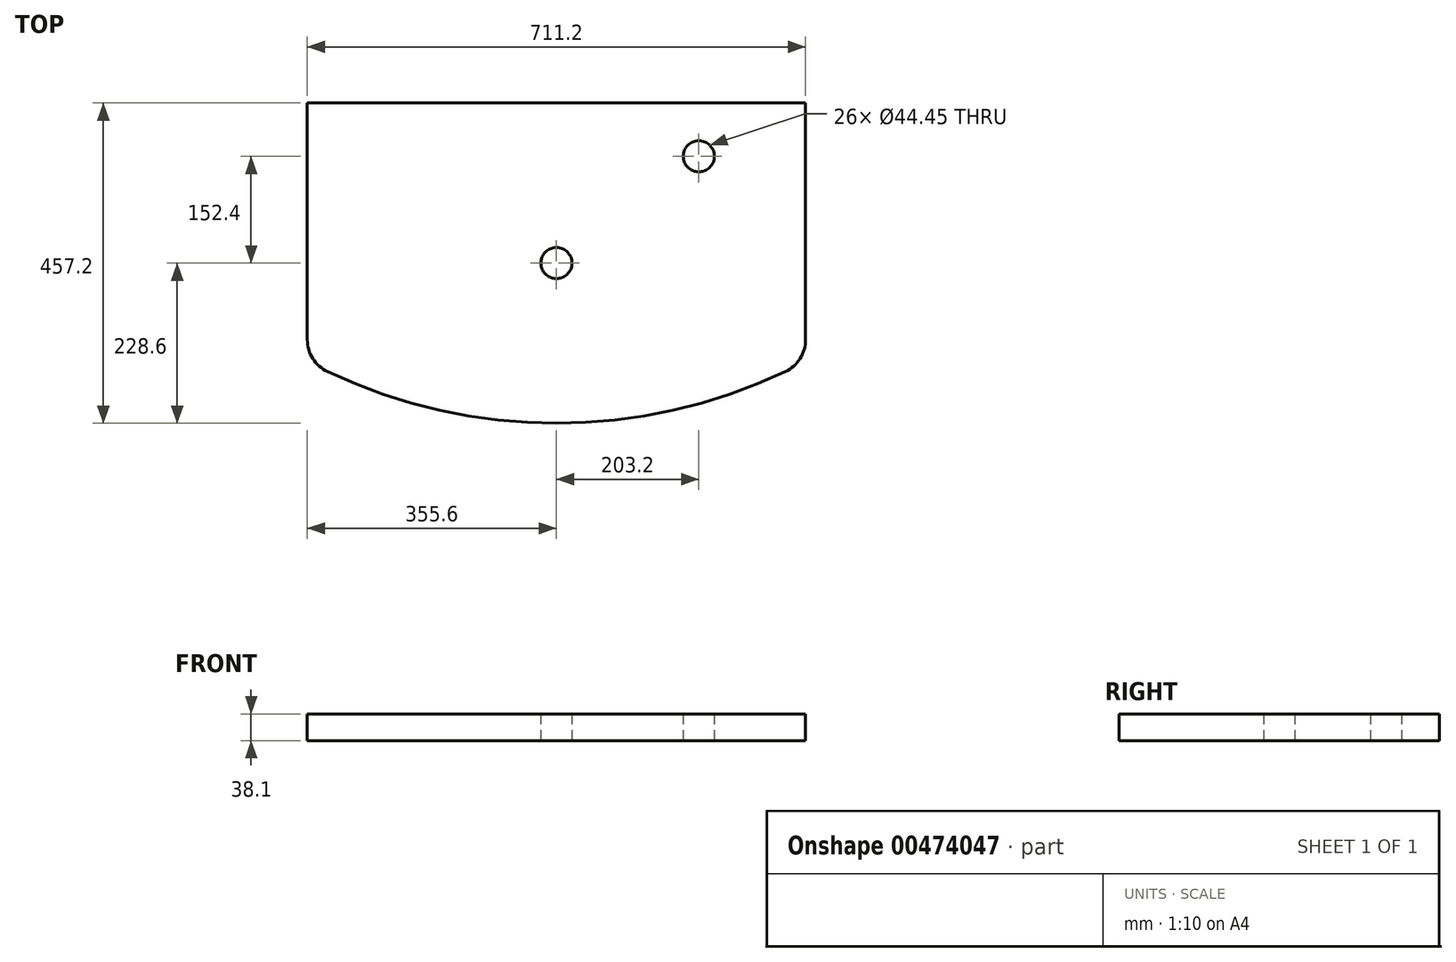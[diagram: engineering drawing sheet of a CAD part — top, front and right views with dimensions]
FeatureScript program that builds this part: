
annotation { "Feature Type Name" : "Feature", "Feature Type Description" : "" }
export const myFeature = defineFeature(function(context is Context, id is Id, definition is map)
    precondition{}
    {
        {
            var Q0;
            Q0=qCreatedBy(makeId("Top.planeOp"),FACE);
            var sketch = newSketch(context, id + "F0", { "sketchPlane" : qUnion([Q0])});
            skLineSegment(sketch, "E0.bottom", {"start": v(558.8, 0) * mm, "end": v(1270, 0) * mm});
            skCircle(sketch, "E1", {"center": v(1117.6, -76.2) * mm, "radius": 22.23 * mm});
            skCircle(sketch, "E2", {"center": v(914.4, -228.6) * mm, "radius": 195.58 * mm, "construction": true});
            skCircle(sketch, "E3", {"center": v(914.4, -228.6) * mm, "radius": 22.23 * mm});
            skArc(sketch, "E4", {"start": v(587.83, -383.67) * mm, "mid": v(914.4, -457.2) * mm, "end": v(1240.97, -383.67) * mm});
            skLineSegment(sketch, "E5", {"start": v(558.8, 0) * mm, "end": v(558.8, -337.77) * mm});
            skLineSegment(sketch, "E6", {"start": v(1270, 0) * mm, "end": v(1270, -337.77) * mm});
            skArc(sketch, "E7.filletArc", {"start": v(1240.97, -383.67) * mm, "mid": v(1262.13, -364.93) * mm, "end": v(1270, -337.77) * mm});
            skArc(sketch, "E8.filletArc", {"start": v(558.8, -337.77) * mm, "mid": v(566.67, -364.93) * mm, "end": v(587.83, -383.67) * mm});
            skSolve(sketch);
        }
        {
            var Q0;
            Q0=makeQuery(id+"F0.imprint","IMPRINT",FACE,{"disambiguationData":[TD([[makeQuery(id+"F0.imprint","IMPRINT",EDGE,{"derivedFrom":sQuery(id+"F0.wireOp",EDGE,"E0.bottom")}),-1.0]])]});
            extrude(context, id + "F1", {"entities" : qUnion([Q0]), "endBound" : BoundingType.SYMMETRIC, "depth" : 38.1 * mm});
        }
    });
